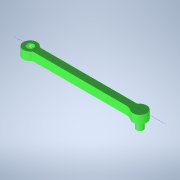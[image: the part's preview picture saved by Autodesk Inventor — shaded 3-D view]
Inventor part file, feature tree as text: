
AUTODESK INVENTOR PART (.ipt)
format: ipt  version: 2022 (Build 260153000, 153)  size: 110,080 bytes
history: imported  units: in
note: dims shown in document units (in); Inventor stores cm internally (conversion verified against a paired STEP export)
features: sketch x1, imported_body x1
ambient origin geometry x8: Origin, YZ Plane, XZ Plane, XY Plane, X Axis, Y Axis, Z Axis, Center Point
bodies: Solid1 (imported_parasolid), Body1 (imported_parasolid)
feature tree (2):
  sketch  "Sketch1"
  imported_body  NMx_Import_Brep_tag  [imported B-rep: ~13 faces, bbox_mm=[240.0, 36.0, 21.748953]]
